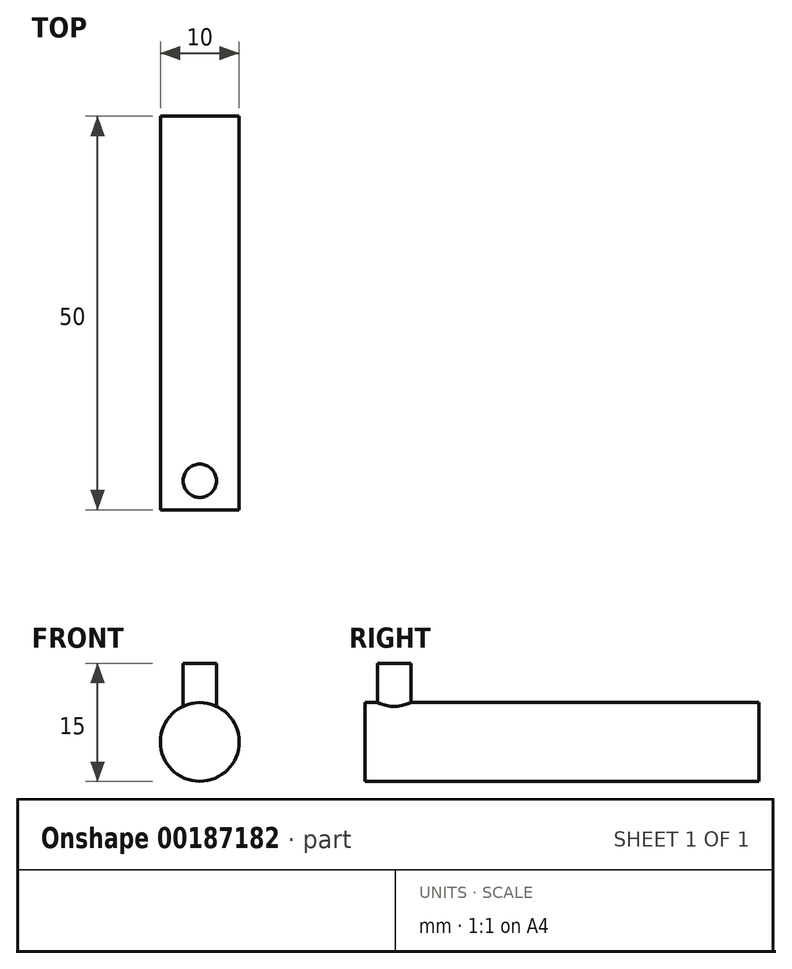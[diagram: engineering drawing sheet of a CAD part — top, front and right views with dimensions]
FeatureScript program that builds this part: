
annotation { "Feature Type Name" : "Feature", "Feature Type Description" : "" }
export const myFeature = defineFeature(function(context is Context, id is Id, definition is map)
    precondition{}
    {
        {
            var Q0;
            Q0=qCreatedBy(makeId("Front.planeOp"),FACE);
            var sketch = newSketch(context, id + "F0", { "sketchPlane" : qUnion([Q0])});
            skCircle(sketch, "E0", {"center": v(0, 0) * mm, "radius": 5 * mm});
            skSolve(sketch);
        }
        {
            var Q0;
            Q0=makeQuery(id+"F0.imprint","IMPRINT",FACE,{"disambiguationData":[TD([[makeQuery(id+"F0.imprint","IMPRINT",EDGE,{"derivedFrom":sQuery(id+"F0.wireOp",EDGE,"E0")}),1.0]])]});
            extrude(context, id + "F1", {"entities" : qUnion([Q0]), "depth" : 50 * mm});
        }
        {
            var Q0;
            Q0=qCreatedBy(makeId("Top.planeOp"),FACE);
            var sketch = newSketch(context, id + "F2", { "sketchPlane" : qUnion([Q0])});
            skCircle(sketch, "E1", {"center": v(0, -46.32) * mm, "radius": 2.12 * mm});
            skSolve(sketch);
        }
        {
            var Q0;
            Q0 = qSketchRegion(id + "F2", true);
            extrude(context, id + "F3", {"entities" : qUnion([Q0]), "operationType" : NewBodyOperationType.ADD, "depth" : 10 * mm});
        }
    });
